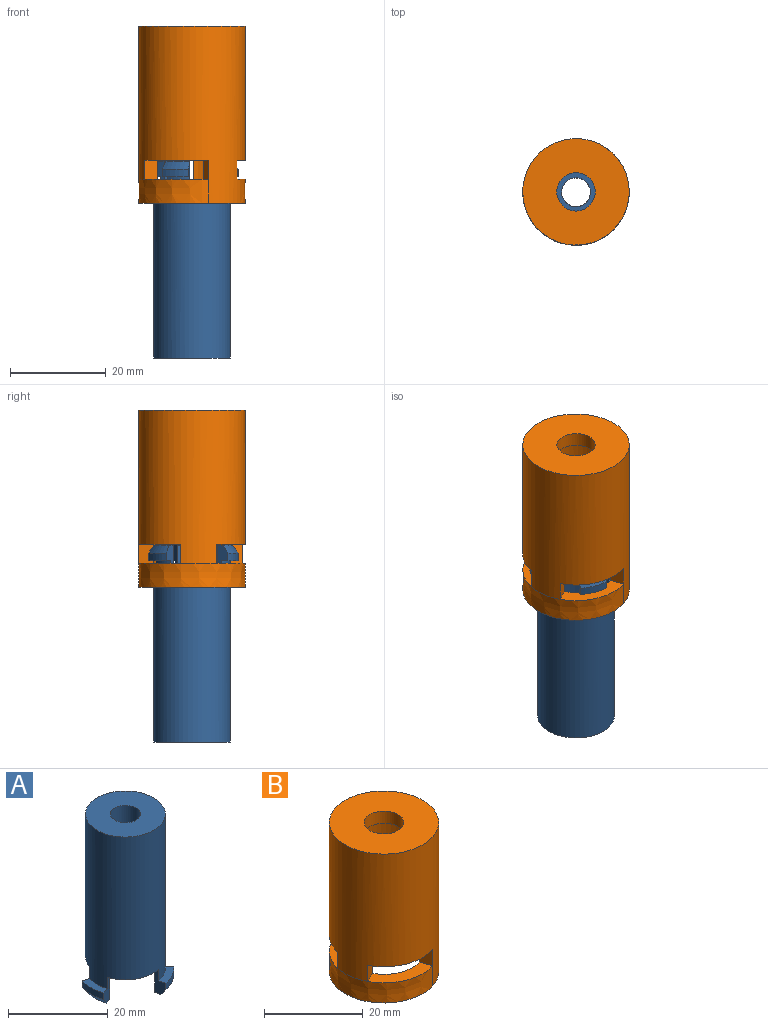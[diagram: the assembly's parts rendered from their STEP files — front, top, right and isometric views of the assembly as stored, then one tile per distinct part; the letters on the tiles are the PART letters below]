
ASSEMBLY  parts=2 mates=1
PART A: 28 faces, bbox 17.7x18.9x41 mm
  f0: plane 4.85x3.62mm, normal (0,0,-1), area 7.2mm2, adj f3,f24,f25,f26
  f1: plane 4.85x3.62mm, normal (0,0,-1), area 7.2mm2, adj f4,f21,f22,f23
  f2: plane 5.25x1.83mm, normal (0,0,-1), area 7.2mm2, adj f5,f18,f19,f20
  f3: cone r=8.49mm half-angle=36.5deg, axis (0,0,1), area 11.5mm2, adj f0,f8,f25,f26
  f4: cone r=8.49mm half-angle=36.5deg, axis (0,0,1), area 11.5mm2, adj f1,f6,f21,f23
  f5: cone r=8.49mm half-angle=36.5deg, axis (0,0,1), area 11.5mm2, adj f2,f7,f19,f20
  f6: cylinder r=9.68mm len=5.18mm, axis (0,0,-1), area 9.6mm2, adj f4,f9,f21,f23
  f7: cylinder r=9.68mm len=5.98mm, axis (0,0,-1), area 9.6mm2, adj f5,f10,f19,f20
  f8: cylinder r=9.68mm len=5.18mm, axis (0,0,-1), area 9.6mm2, adj f3,f25,f26,f27
  f9: plane 5.53x4.12mm, normal (0,0,1), area 9.3mm2, adj f6,f11,f21,f23
  f10: plane 5.98x2.07mm, normal (0,0,1), area 9.3mm2, adj f7,f11,f19,f20
  f11: cylinder r=8mm len=37.8mm, axis (0,0,-1), area 1801.6mm2, adj f9,f10,f12,f13,f14,f15,f19,f20
  f12: plane 10.71x2.8mm, normal (0,0,-1), area 11mm2, adj f11,f16,f21,f25
  f13: plane 9.27x5.84mm, normal (0,0,-1), area 11mm2, adj f11,f16,f20,f23
  f14: plane 16x16mm, normal (0,0,1), area 172.8mm2, adj f11,f17
  f15: plane 9.27x5.84mm, normal (0,0,-1), area 11mm2, adj f11,f16,f19,f26
  f16: cone r=7mm half-angle=20deg, axis (0,0,-1), area 367.4mm2, adj f12,f13,f15,f17,f18,f22,f24
  f17: cylinder r=3mm len=24.01mm, axis (0,0,1), area 452.6mm2, adj f14,f16
  f18: cylinder r=7mm len=6mm, axis (0,0,1), area 26.4mm2, adj f2,f16,f19,f20
  f19: plane 6x2.55mm, normal (0.31,-0.95,0), area 10.4mm2, adj f2,f5,f7,f10,f11,f15,f18
  f20: plane 6x2.55mm, normal (0.31,0.95,0), area 10.4mm2, adj f2,f5,f7,f10,f11,f13,f18
  f21: plane 6x1.99mm, normal (0.67,-0.74,0), area 10.4mm2, adj f1,f4,f6,f9,f11,f12,f22
  f22: cylinder r=7mm len=6mm, axis (0,0,1), area 26.4mm2, adj f1,f16,f21,f23
  f23: plane 6x2.62mm, normal (-0.98,0.21,0), area 10.4mm2, adj f1,f4,f6,f9,f11,f13,f22
  f24: cylinder r=7mm len=6mm, axis (0,0,1), area 26.4mm2, adj f0,f16,f25,f26
  f25: plane 6x1.99mm, normal (0.67,0.74,0), area 10.4mm2, adj f0,f3,f8,f11,f12,f24,f27
  f26: plane 6x2.62mm, normal (-0.98,-0.21,0), area 10.4mm2, adj f0,f3,f8,f11,f15,f24,f27
  f27: plane 5.53x4.12mm, normal (0,0,1), area 9.3mm2, adj f8,f11,f25,f26
PART B: 20 faces, bbox 22.2x22.2x37 mm
  f0: plane 13.2x7.34mm, normal (0,0,-1), area 40.2mm2, adj f2,f3,f9,f12
  f1: plane 11.3x9.37mm, normal (0,0,-1), area 40.2mm2, adj f2,f3,f10,f13
  f2: cylinder r=8.1mm len=34mm, axis (0,0,-1), area 1368.5mm2, adj f0,f1,f4,f5,f8,f9,f10,f11
  f3: cylinder r=11.1mm len=37mm, axis (0,0,-1), area 2084.6mm2, adj f0,f1,f4,f7,f8,f9,f10,f11
  f4: plane 14.14x5.64mm, normal (0,0,-1), area 40.2mm2, adj f2,f3,f8,f11
  f5: plane 16.2x16.2mm, normal (0,0,-1), area 155.9mm2, adj f2,f6
  f6: cylinder r=4mm len=8mm, axis (0,0,-1), area 75.4mm2, adj f5,f7
  f7: plane 22.2x22.2mm, normal (0,0,1), area 336.8mm2, adj f3,f6
  f8: plane 4x2.53mm, normal (0.54,0.84,0), area 12mm2, adj f2,f3,f4,f15
  f9: plane 4x2.86mm, normal (-0.95,-0.3,0), area 12mm2, adj f0,f2,f3,f14
  f10: plane 4x3mm, normal (-1,0.04,0), area 12mm2, adj f1,f2,f3,f19
  f11: plane 4x2.22mm, normal (0.74,-0.67,0), area 12mm2, adj f2,f3,f4,f15
  f12: plane 4x2.66mm, normal (0.46,-0.89,0), area 12mm2, adj f0,f2,f3,f14
  f13: plane 4x2.93mm, normal (0.21,0.98,0), area 12mm2, adj f1,f2,f3,f19
  f14: plane 13.2x7.35mm, normal (0,0,1), area 40.2mm2, adj f9,f12,f16,f17
  f15: plane 14.15x5.65mm, normal (0,0,1), area 40.2mm2, adj f8,f11,f16,f17
  f16: extruded ~16.19x16.19mm, area 226.2mm2, adj f2,f14,f15,f18,f19
  f17: extruded ~22.18x22.18mm, area 310mm2, adj f3,f14,f15,f18,f19
  f18: plane 22.21x22.21mm, normal (0,0,-1), area 181mm2, adj f2,f3,f16,f17
  f19: plane 11.31x9.37mm, normal (0,0,1), area 40.2mm2, adj f10,f13,f16,f17
PLACE A rot(axis=(0.83,0.56,0),180deg) t=(0.13,9.3,-6.25)mm
PLACE B t=(0.13,9.3,0)mm fixed
MATE cylindrical A.f11 <-> B.f3  axis (0,0,1) through (0.13,9.3,-22.34)mm
